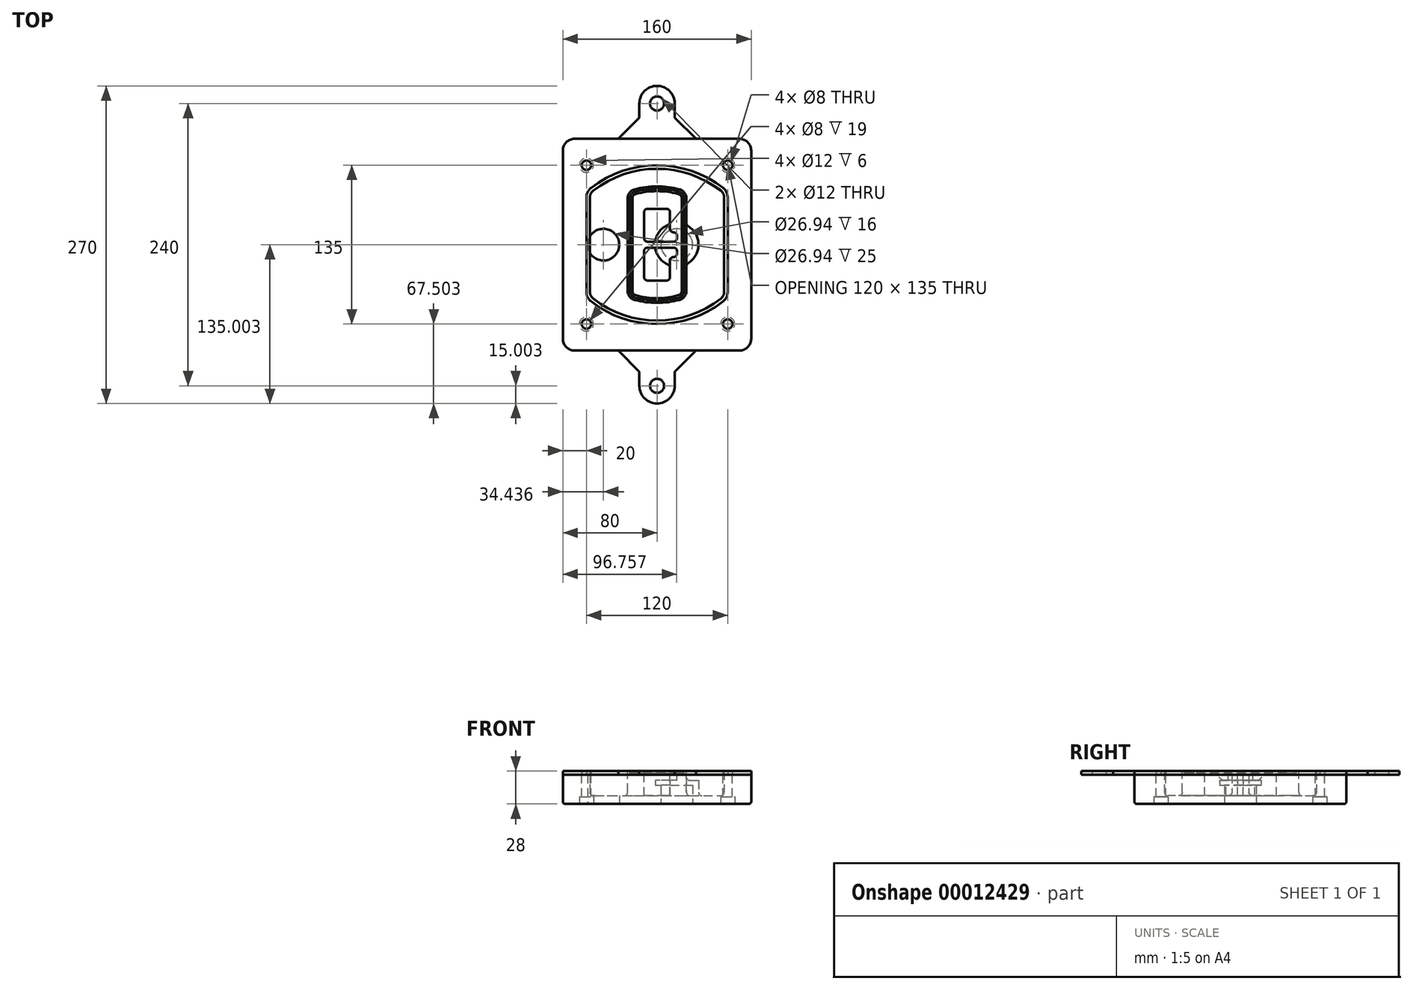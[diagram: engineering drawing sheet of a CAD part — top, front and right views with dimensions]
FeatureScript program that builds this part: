
annotation { "Feature Type Name" : "Feature", "Feature Type Description" : "" }
export const myFeature = defineFeature(function(context is Context, id is Id, definition is map)
    precondition{}
    {
        {
            var Q0;
            Q0=qCreatedBy(makeId("Top.planeOp"),FACE);
            var sketch = newSketch(context, id + "F0", { "sketchPlane" : qUnion([Q0])});
            skPoint(sketch, "E0.rect.middle", {"position": v(0, 0) * mm});
            skLineSegment(sketch, "E1.bottom", {"start": v(24.05, 28.38) * mm, "end": v(164.05, 28.38) * mm});
            skLineSegment(sketch, "E1.top", {"start": v(24.05, 208.38) * mm, "end": v(164.05, 208.38) * mm});
            skLineSegment(sketch, "E1.left", {"start": v(14.05, 38.38) * mm, "end": v(14.05, 198.38) * mm});
            skLineSegment(sketch, "E1.right", {"start": v(174.05, 38.38) * mm, "end": v(174.05, 198.38) * mm});
            skLineSegment(sketch, "E2", {"start": v(14.05, 208.38) * mm, "end": v(174.05, 28.38) * mm, "construction": true});
            skLineSegment(sketch, "E3", {"start": v(174.05, 208.38) * mm, "end": v(14.05, 28.38) * mm, "construction": true});
            skCircle(sketch, "E4", {"center": v(34.05, 185.88) * mm, "radius": 4 * mm});
            skCircle(sketch, "E5", {"center": v(154.05, 185.88) * mm, "radius": 4 * mm});
            skCircle(sketch, "E6", {"center": v(154.05, 50.88) * mm, "radius": 4 * mm});
            skCircle(sketch, "E7", {"center": v(34.05, 50.88) * mm, "radius": 4 * mm});
            skLineSegment(sketch, "E8", {"start": v(34.05, 185.88) * mm, "end": v(154.05, 185.88) * mm, "construction": true});
            skLineSegment(sketch, "E9", {"start": v(154.05, 185.88) * mm, "end": v(154.05, 50.88) * mm, "construction": true});
            skLineSegment(sketch, "E10", {"start": v(154.05, 50.88) * mm, "end": v(34.05, 50.88) * mm, "construction": true});
            skLineSegment(sketch, "E11", {"start": v(34.05, 50.88) * mm, "end": v(34.05, 185.88) * mm, "construction": true});
            skLineSegment(sketch, "E12", {"start": v(34.05, 158.68) * mm, "end": v(34.05, 78.09) * mm});
            skLineSegment(sketch, "E13", {"start": v(154.05, 158.68) * mm, "end": v(154.05, 78.09) * mm});
            skArc(sketch, "E14", {"start": v(150.2, 166.56) * mm, "mid": v(94.05, 185.88) * mm, "end": v(37.9, 166.56) * mm});
            skArc(sketch, "E15", {"start": v(37.9, 70.2) * mm, "mid": v(94.05, 50.88) * mm, "end": v(150.2, 70.2) * mm});
            skLineSegment(sketch, "E16", {"start": v(34.05, 118.38) * mm, "end": v(154.05, 118.38) * mm, "construction": true});
            skPoint(sketch, "E17.visualSharp", {"position": v(34.05, 73.38) * mm});
            skArc(sketch, "E17.filletArc", {"start": v(34.05, 78.09) * mm, "mid": v(35.06, 73.7) * mm, "end": v(37.9, 70.2) * mm});
            skPoint(sketch, "E18.visualSharp", {"position": v(34.05, 163.38) * mm});
            skArc(sketch, "E18.filletArc", {"start": v(37.9, 166.56) * mm, "mid": v(35.06, 163.06) * mm, "end": v(34.05, 158.68) * mm});
            skPoint(sketch, "E19.visualSharp", {"position": v(154.05, 163.38) * mm});
            skArc(sketch, "E19.filletArc", {"start": v(154.05, 158.68) * mm, "mid": v(153.04, 163.06) * mm, "end": v(150.2, 166.56) * mm});
            skPoint(sketch, "E20.visualSharp", {"position": v(154.05, 73.38) * mm});
            skArc(sketch, "E20.filletArc", {"start": v(150.2, 70.2) * mm, "mid": v(153.04, 73.7) * mm, "end": v(154.05, 78.09) * mm});
            skPoint(sketch, "E21.visualSharp", {"position": v(14.05, 208.38) * mm});
            skArc(sketch, "E21.filletArc", {"start": v(24.05, 208.38) * mm, "mid": v(16.98, 205.45) * mm, "end": v(14.05, 198.38) * mm});
            skPoint(sketch, "E22.visualSharp", {"position": v(174.05, 208.38) * mm});
            skArc(sketch, "E22.filletArc", {"start": v(174.05, 198.38) * mm, "mid": v(171.12, 205.45) * mm, "end": v(164.05, 208.38) * mm});
            skPoint(sketch, "E23.visualSharp", {"position": v(174.05, 28.38) * mm});
            skArc(sketch, "E23.filletArc", {"start": v(164.05, 28.38) * mm, "mid": v(171.12, 31.31) * mm, "end": v(174.05, 38.38) * mm});
            skPoint(sketch, "E24.visualSharp", {"position": v(14.05, 28.38) * mm});
            skArc(sketch, "E24.filletArc", {"start": v(14.05, 38.38) * mm, "mid": v(16.98, 31.31) * mm, "end": v(24.05, 28.38) * mm});
            skArc(sketch, "E25.0", {"start": v(151.05, 158.68) * mm, "mid": v(150.34, 161.75) * mm, "end": v(148.36, 164.2) * mm});
            skLineSegment(sketch, "E25.1", {"start": v(151.05, 158.68) * mm, "end": v(151.05, 78.09) * mm});
            skArc(sketch, "E25.2", {"start": v(148.36, 72.57) * mm, "mid": v(150.34, 75.02) * mm, "end": v(151.05, 78.09) * mm});
            skArc(sketch, "E25.3", {"start": v(39.74, 72.57) * mm, "mid": v(94.05, 53.88) * mm, "end": v(148.36, 72.57) * mm});
            skArc(sketch, "E25.4", {"start": v(37.05, 78.09) * mm, "mid": v(37.76, 75.02) * mm, "end": v(39.74, 72.57) * mm});
            skArc(sketch, "E25.5", {"start": v(148.36, 164.2) * mm, "mid": v(94.05, 182.88) * mm, "end": v(39.74, 164.2) * mm});
            skLineSegment(sketch, "E25.6", {"start": v(37.05, 158.68) * mm, "end": v(37.05, 78.09) * mm});
            skArc(sketch, "E25.7", {"start": v(39.74, 164.2) * mm, "mid": v(37.76, 161.75) * mm, "end": v(37.05, 158.68) * mm});
            skArc(sketch, "E26.0", {"start": v(35.43, 169.71) * mm, "mid": v(31.47, 164.82) * mm, "end": v(30.05, 158.68) * mm});
            skArc(sketch, "E26.1", {"start": v(152.67, 169.71) * mm, "mid": v(94.05, 189.88) * mm, "end": v(35.43, 169.71) * mm});
            skArc(sketch, "E26.2", {"start": v(158.05, 158.68) * mm, "mid": v(156.63, 164.82) * mm, "end": v(152.67, 169.71) * mm});
            skLineSegment(sketch, "E26.3", {"start": v(158.05, 158.68) * mm, "end": v(158.05, 78.09) * mm});
            skArc(sketch, "E26.4", {"start": v(152.67, 67.05) * mm, "mid": v(156.63, 71.95) * mm, "end": v(158.05, 78.09) * mm});
            skLineSegment(sketch, "E26.5", {"start": v(30.05, 158.68) * mm, "end": v(30.05, 78.09) * mm});
            skArc(sketch, "E26.6", {"start": v(35.43, 67.05) * mm, "mid": v(94.05, 46.88) * mm, "end": v(152.67, 67.05) * mm});
            skArc(sketch, "E26.7", {"start": v(30.05, 78.09) * mm, "mid": v(31.47, 71.95) * mm, "end": v(35.43, 67.05) * mm});
            skSolve(sketch);
        }
        {
            var Q0;
            Q0=makeQuery(id+"F0.imprint","IMPRINT",FACE,{"disambiguationData":[TD([[makeQuery(id+"F0.imprint","IMPRINT",EDGE,{"derivedFrom":sQuery(id+"F0.wireOp",EDGE,"E1.bottom")}),1.0]])]});
            var Q1;
            Q1=makeQuery(id+"F0.imprint","IMPRINT",FACE,{"disambiguationData":[TD([[makeQuery(id+"F0.imprint","IMPRINT",EDGE,{"derivedFrom":sQuery(id+"F0.wireOp",EDGE,"E12")}),1.0]])]});
            var Q2;
            Q2=makeQuery(id+"F0.imprint","IMPRINT",FACE,{"disambiguationData":[TD([[makeQuery(id+"F0.imprint","IMPRINT",EDGE,{"derivedFrom":sQuery(id+"F0.wireOp",EDGE,"E25.0")}),1.0]])]});
            var Q3;
            Q3=makeQuery(id+"F0.imprint","IMPRINT",FACE,{"disambiguationData":[TD([[makeQuery(id+"F0.imprint","IMPRINT",EDGE,{"derivedFrom":sQuery(id+"F0.wireOp",EDGE,"E12")}),-1.0]])]});
            extrude(context, id + "F1", {"entities" : qUnion([Q0, Q1, Q2, Q3]), "oppositeDirection" : true, "depth" : 25 * mm});
        }
        {
            var Q0;
            Q0=makeQuery(id+"F0.imprint","IMPRINT",FACE,{"disambiguationData":[TD([[makeQuery(id+"F0.imprint","IMPRINT",EDGE,{"derivedFrom":sQuery(id+"F0.wireOp",EDGE,"E12")}),1.0]])]});
            extrude(context, id + "F2", {"entities" : qUnion([Q0]), "operationType" : NewBodyOperationType.ADD, "depth" : 3 * mm});
        }
        {
            var Q0;
            Q0=makeQuery(id+"F0.imprint","IMPRINT",FACE,{"disambiguationData":[TD([[makeQuery(id+"F0.imprint","IMPRINT",EDGE,{"derivedFrom":sQuery(id+"F0.wireOp",EDGE,"E25.0")}),1.0]])]});
            extrude(context, id + "F3", {"entities" : qUnion([Q0]), "operationType" : NewBodyOperationType.REMOVE, "oppositeDirection" : true, "depth" : 18 * mm});
        }
        {
            var Q0;
            Q0=makeQuery(id+"F2.opExtrude","CAP_FACE",FACE,{"disambiguationData":[OSD([sQuery(id+"F0.wireOp",EDGE,"E12"),sQuery(id+"F0.wireOp",EDGE,"E13"),sQuery(id+"F0.wireOp",EDGE,"E14"),sQuery(id+"F0.wireOp",EDGE,"E15"),sQuery(id+"F0.wireOp",EDGE,"E17.filletArc"),sQuery(id+"F0.wireOp",EDGE,"E18.filletArc"),sQuery(id+"F0.wireOp",EDGE,"E19.filletArc"),sQuery(id+"F0.wireOp",EDGE,"E20.filletArc"),sQuery(id+"F0.wireOp",EDGE,"E25.0"),sQuery(id+"F0.wireOp",EDGE,"E25.1"),sQuery(id+"F0.wireOp",EDGE,"E25.2"),sQuery(id+"F0.wireOp",EDGE,"E25.3"),sQuery(id+"F0.wireOp",EDGE,"E25.4"),sQuery(id+"F0.wireOp",EDGE,"E25.5"),sQuery(id+"F0.wireOp",EDGE,"E25.6"),sQuery(id+"F0.wireOp",EDGE,"E25.7")])],"isStart":false});
            var sketch = newSketch(context, id + "F4", { "sketchPlane" : qUnion([Q0])});
            skArc(sketch, "E27.0", {"start": v(74.97, 71.41) * mm, "mid": v(94.05, 68.88) * mm, "end": v(113.13, 71.41) * mm});
            skArc(sketch, "E28.0", {"start": v(113.13, 165.35) * mm, "mid": v(94.05, 167.88) * mm, "end": v(74.97, 165.35) * mm});
            skLineSegment(sketch, "E29", {"start": v(69.05, 157.63) * mm, "end": v(69.05, 79.14) * mm});
            skLineSegment(sketch, "E30", {"start": v(119.05, 157.63) * mm, "end": v(119.05, 79.14) * mm});
            skLineSegment(sketch, "E31", {"start": v(69.05, 163.48) * mm, "end": v(119.05, 163.48) * mm, "construction": true});
            skLineSegment(sketch, "E32", {"start": v(69.05, 73.28) * mm, "end": v(119.05, 73.28) * mm, "construction": true});
            skPoint(sketch, "E33.visualSharp", {"position": v(69.05, 163.48) * mm});
            skArc(sketch, "E33.filletArc", {"start": v(74.97, 165.35) * mm, "mid": v(70.7, 162.5) * mm, "end": v(69.05, 157.63) * mm});
            skPoint(sketch, "E34.visualSharp", {"position": v(119.05, 163.48) * mm});
            skArc(sketch, "E34.filletArc", {"start": v(119.05, 157.63) * mm, "mid": v(117.4, 162.5) * mm, "end": v(113.13, 165.35) * mm});
            skPoint(sketch, "E35.visualSharp", {"position": v(119.05, 73.28) * mm});
            skArc(sketch, "E35.filletArc", {"start": v(113.13, 71.41) * mm, "mid": v(117.4, 74.27) * mm, "end": v(119.05, 79.14) * mm});
            skPoint(sketch, "E36.visualSharp", {"position": v(69.05, 73.28) * mm});
            skArc(sketch, "E36.filletArc", {"start": v(69.05, 79.14) * mm, "mid": v(70.7, 74.27) * mm, "end": v(74.97, 71.41) * mm});
            skArc(sketch, "E37.0", {"start": v(148.36, 164.2) * mm, "mid": v(94.05, 182.88) * mm, "end": v(39.74, 164.2) * mm});
            skArc(sketch, "E37.1", {"start": v(39.74, 164.2) * mm, "mid": v(37.76, 161.75) * mm, "end": v(37.05, 158.68) * mm});
            skLineSegment(sketch, "E37.2", {"start": v(37.05, 158.68) * mm, "end": v(37.05, 78.09) * mm});
            skArc(sketch, "E37.3", {"start": v(37.05, 78.09) * mm, "mid": v(37.76, 75.02) * mm, "end": v(39.74, 72.57) * mm});
            skArc(sketch, "E37.4", {"start": v(39.74, 72.57) * mm, "mid": v(94.05, 53.88) * mm, "end": v(148.36, 72.57) * mm});
            skArc(sketch, "E37.5", {"start": v(148.36, 72.57) * mm, "mid": v(150.34, 75.02) * mm, "end": v(151.05, 78.09) * mm});
            skLineSegment(sketch, "E37.6", {"start": v(151.05, 158.68) * mm, "end": v(151.05, 78.09) * mm});
            skArc(sketch, "E37.7", {"start": v(151.05, 158.68) * mm, "mid": v(150.34, 161.75) * mm, "end": v(148.36, 164.2) * mm});
            skLineSegment(sketch, "E38.0", {"start": v(117.05, 157.63) * mm, "end": v(117.05, 79.14) * mm});
            skArc(sketch, "E38.1", {"start": v(112.61, 73.34) * mm, "mid": v(115.81, 75.49) * mm, "end": v(117.05, 79.14) * mm});
            skArc(sketch, "E38.2", {"start": v(75.49, 73.34) * mm, "mid": v(94.05, 70.88) * mm, "end": v(112.61, 73.34) * mm});
            skArc(sketch, "E38.3", {"start": v(71.05, 79.14) * mm, "mid": v(72.29, 75.49) * mm, "end": v(75.49, 73.34) * mm});
            skLineSegment(sketch, "E38.4", {"start": v(71.05, 157.63) * mm, "end": v(71.05, 79.14) * mm});
            skArc(sketch, "E38.5", {"start": v(117.05, 157.63) * mm, "mid": v(115.81, 161.28) * mm, "end": v(112.61, 163.42) * mm});
            skArc(sketch, "E38.6", {"start": v(75.49, 163.42) * mm, "mid": v(72.29, 161.28) * mm, "end": v(71.05, 157.63) * mm});
            skArc(sketch, "E38.7", {"start": v(112.61, 163.42) * mm, "mid": v(94.05, 165.88) * mm, "end": v(75.49, 163.42) * mm});
            skArc(sketch, "E39.0", {"start": v(115.05, 157.63) * mm, "mid": v(114.23, 160.06) * mm, "end": v(112.1, 161.5) * mm});
            skLineSegment(sketch, "E39.1", {"start": v(115.05, 157.63) * mm, "end": v(115.05, 79.14) * mm});
            skArc(sketch, "E39.2", {"start": v(112.1, 75.27) * mm, "mid": v(114.23, 76.7) * mm, "end": v(115.05, 79.14) * mm});
            skArc(sketch, "E39.3", {"start": v(76, 75.27) * mm, "mid": v(94.05, 72.88) * mm, "end": v(112.1, 75.27) * mm});
            skArc(sketch, "E39.4", {"start": v(73.05, 79.14) * mm, "mid": v(73.87, 76.7) * mm, "end": v(76, 75.27) * mm});
            skArc(sketch, "E39.5", {"start": v(112.1, 161.5) * mm, "mid": v(94.05, 163.88) * mm, "end": v(76, 161.5) * mm});
            skLineSegment(sketch, "E39.6", {"start": v(73.05, 157.63) * mm, "end": v(73.05, 79.14) * mm});
            skArc(sketch, "E39.7", {"start": v(76, 161.5) * mm, "mid": v(73.87, 160.06) * mm, "end": v(73.05, 157.63) * mm});
            skLineSegment(sketch, "E40", {"start": v(69.05, 118.38) * mm, "end": v(119.05, 118.38) * mm, "construction": true});
            skLineSegment(sketch, "E41", {"start": v(83.05, 123.88) * mm, "end": v(83.05, 145.88) * mm});
            skLineSegment(sketch, "E42", {"start": v(86.05, 148.88) * mm, "end": v(102.05, 148.88) * mm});
            skLineSegment(sketch, "E43", {"start": v(105.05, 145.88) * mm, "end": v(105.05, 131.88) * mm});
            skLineSegment(sketch, "E44", {"start": v(108.05, 128.88) * mm, "end": v(108.05, 128.88) * mm});
            skLineSegment(sketch, "E45", {"start": v(111.05, 125.88) * mm, "end": v(111.05, 123.88) * mm});
            skLineSegment(sketch, "E46", {"start": v(108.05, 120.88) * mm, "end": v(86.05, 120.88) * mm});
            skPoint(sketch, "E47.visualSharp", {"position": v(83.05, 148.88) * mm});
            skArc(sketch, "E47.filletArc", {"start": v(86.05, 148.88) * mm, "mid": v(83.93, 148) * mm, "end": v(83.05, 145.88) * mm});
            skPoint(sketch, "E48.visualSharp", {"position": v(105.05, 148.88) * mm});
            skArc(sketch, "E48.filletArc", {"start": v(105.05, 145.88) * mm, "mid": v(104.17, 148) * mm, "end": v(102.05, 148.88) * mm});
            skPoint(sketch, "E49.visualSharp", {"position": v(105.05, 128.88) * mm});
            skArc(sketch, "E49.filletArc", {"start": v(105.05, 131.88) * mm, "mid": v(105.93, 129.76) * mm, "end": v(108.05, 128.88) * mm});
            skPoint(sketch, "E50.visualSharp", {"position": v(111.05, 128.88) * mm});
            skArc(sketch, "E50.filletArc", {"start": v(111.05, 125.88) * mm, "mid": v(110.17, 128) * mm, "end": v(108.05, 128.88) * mm});
            skPoint(sketch, "E51.visualSharp", {"position": v(111.05, 120.88) * mm});
            skArc(sketch, "E51.filletArc", {"start": v(108.05, 120.88) * mm, "mid": v(110.17, 121.76) * mm, "end": v(111.05, 123.88) * mm});
            skPoint(sketch, "E52.visualSharp", {"position": v(83.05, 120.88) * mm});
            skArc(sketch, "E52.filletArc", {"start": v(83.05, 123.88) * mm, "mid": v(83.93, 121.76) * mm, "end": v(86.05, 120.88) * mm});
            skLineSegment(sketch, "E53.0.MirrorCS", {"start": v(108.05, 115.88) * mm, "end": v(86.05, 115.88) * mm});
            skArc(sketch, "E54.0.MirrorCS", {"start": v(83.05, 112.88) * mm, "mid": v(83.93, 115) * mm, "end": v(86.05, 115.88) * mm});
            skLineSegment(sketch, "E55.0.MirrorCS", {"start": v(83.05, 112.88) * mm, "end": v(83.05, 90.88) * mm});
            skArc(sketch, "E56.0.MirrorCS", {"start": v(86.05, 87.88) * mm, "mid": v(83.93, 88.76) * mm, "end": v(83.05, 90.88) * mm});
            skLineSegment(sketch, "E57.0.MirrorCS", {"start": v(86.05, 87.88) * mm, "end": v(102.05, 87.88) * mm});
            skArc(sketch, "E58.0.MirrorCS", {"start": v(105.05, 90.88) * mm, "mid": v(104.17, 88.76) * mm, "end": v(102.05, 87.88) * mm});
            skLineSegment(sketch, "E59.0.MirrorCS", {"start": v(105.05, 90.88) * mm, "end": v(105.05, 104.88) * mm});
            skArc(sketch, "E60.0.MirrorCS", {"start": v(105.05, 104.88) * mm, "mid": v(105.93, 107) * mm, "end": v(108.05, 107.88) * mm});
            skArc(sketch, "E61.0.MirrorCS", {"start": v(111.05, 110.88) * mm, "mid": v(110.17, 108.76) * mm, "end": v(108.05, 107.88) * mm});
            skLineSegment(sketch, "E62.0.MirrorCS", {"start": v(111.05, 110.88) * mm, "end": v(111.05, 112.88) * mm});
            skArc(sketch, "E63.0.MirrorCS", {"start": v(108.05, 115.88) * mm, "mid": v(110.17, 115) * mm, "end": v(111.05, 112.88) * mm});
            skSolve(sketch);
        }
        {
            var Q0;
            Q0=makeQuery(id+"F4.imprint","IMPRINT",FACE,{"disambiguationData":[TD([[makeQuery(id+"F4.imprint","IMPRINT",EDGE,{"derivedFrom":sQuery(id+"F4.wireOp",EDGE,"E27.0")}),1.0]])]});
            var Q1;
            Q1=makeQuery(id+"F4.imprint","IMPRINT",FACE,{"disambiguationData":[TD([[makeQuery(id+"F4.imprint","IMPRINT",EDGE,{"derivedFrom":sQuery(id+"F4.wireOp",EDGE,"E38.0")}),-1.0]])]});
            var Q2;
            Q2=makeQuery(id+"F4.imprint","IMPRINT",FACE,{"disambiguationData":[TD([[makeQuery(id+"F4.imprint","IMPRINT",EDGE,{"derivedFrom":sQuery(id+"F4.wireOp",EDGE,"E39.0")}),1.0]])]});
            extrude(context, id + "F5", {"entities" : qUnion([Q0, Q1, Q2]), "operationType" : NewBodyOperationType.ADD, "endBound" : BoundingType.UP_TO_NEXT, "oppositeDirection" : true, "depth" : 25 * mm});
        }
        {
            var Q0;
            Q0=makeQuery(id+"F4.imprint","IMPRINT",FACE,{"disambiguationData":[TD([[makeQuery(id+"F4.imprint","IMPRINT",EDGE,{"derivedFrom":sQuery(id+"F4.wireOp",EDGE,"E38.0")}),-1.0]])]});
            extrude(context, id + "F6", {"entities" : qUnion([Q0]), "operationType" : NewBodyOperationType.REMOVE, "oppositeDirection" : true, "depth" : 2 * mm});
        }
        {
            var Q0;
            Q0=makeQuery(id+"F1.opExtrude","CAP_FACE",FACE,{"disambiguationData":[OSD([sQuery(id+"F0.wireOp",EDGE,"E1.bottom"),sQuery(id+"F0.wireOp",EDGE,"E1.top"),sQuery(id+"F0.wireOp",EDGE,"E1.left"),sQuery(id+"F0.wireOp",EDGE,"E1.right"),sQuery(id+"F0.wireOp",EDGE,"E4"),sQuery(id+"F0.wireOp",EDGE,"E5"),sQuery(id+"F0.wireOp",EDGE,"E6"),sQuery(id+"F0.wireOp",EDGE,"E7"),sQuery(id+"F0.wireOp",EDGE,"E21.filletArc"),sQuery(id+"F0.wireOp",EDGE,"E22.filletArc"),sQuery(id+"F0.wireOp",EDGE,"E23.filletArc"),sQuery(id+"F0.wireOp",EDGE,"E24.filletArc")])],"isStart":false});
            var sketch = newSketch(context, id + "F7", { "sketchPlane" : qUnion([Q0])});
            skCircle(sketch, "E64", {"center": v(110.8, -118.38) * mm, "radius": 13.47 * mm});
            skCircle(sketch, "E65", {"center": v(48.49, -118.38) * mm, "radius": 13.47 * mm});
            skLineSegment(sketch, "E66", {"start": v(174.05, -118.38) * mm, "end": v(14.05, -118.38) * mm});
            skCircle(sketch, "E67", {"center": v(110.8, -118.38) * mm, "radius": 18.47 * mm});
            skCircle(sketch, "E68", {"center": v(154.05, -185.88) * mm, "radius": 6 * mm});
            skCircle(sketch, "E69", {"center": v(34.05, -185.88) * mm, "radius": 6 * mm});
            skCircle(sketch, "E70", {"center": v(34.05, -50.88) * mm, "radius": 6 * mm});
            skCircle(sketch, "E71", {"center": v(154.05, -50.88) * mm, "radius": 6 * mm});
            skSolve(sketch);
        }
        {
            var Q0;
            {var subQ1=sQuery(id+"F7.wireOp",EDGE,"E66");var subQ4=sQuery(id+"F7.wireOp",EDGE,"E64");var subQ6=makeQuery(id+"F7.imprint","INTERSECT",VERTEX,{"disambiguationData":[OD(0.0)],"derivedFrom":[subQ4,subQ1]});Q0=makeQuery(id+"F7.imprint","IMPRINT",FACE,{"disambiguationData":[TD([[makeQuery(id+"F7.imprint","IMPRINT",EDGE,{"disambiguationData":[TD([[subQ6,-1.0]])],"derivedFrom":subQ4}),-1.0]])]});}
            var Q1;
            {var subQ0=sQuery(id+"F7.wireOp",EDGE,"E66");var subQ1=sQuery(id+"F7.wireOp",EDGE,"E64");var subQ3=makeQuery(id+"F7.imprint","INTERSECT",VERTEX,{"disambiguationData":[OD(0.0)],"derivedFrom":[subQ1,subQ0]});Q1=makeQuery(id+"F7.imprint","IMPRINT",FACE,{"disambiguationData":[TD([[makeQuery(id+"F7.imprint","IMPRINT",EDGE,{"disambiguationData":[TD([[subQ3,-1.0]])],"derivedFrom":subQ1}),1.0]])]});}
            var Q2;
            {var subQ0=sQuery(id+"F7.wireOp",EDGE,"E66");var subQ1=sQuery(id+"F7.wireOp",EDGE,"E64");var subQ3=makeQuery(id+"F7.imprint","INTERSECT",VERTEX,{"disambiguationData":[OD(0.0)],"derivedFrom":[subQ1,subQ0]});Q2=makeQuery(id+"F7.imprint","IMPRINT",FACE,{"disambiguationData":[TD([[makeQuery(id+"F7.imprint","IMPRINT",EDGE,{"disambiguationData":[TD([[subQ3,1.0]])],"derivedFrom":subQ1}),1.0]])]});}
            var Q3;
            {var subQ1=sQuery(id+"F7.wireOp",EDGE,"E66");var subQ4=sQuery(id+"F7.wireOp",EDGE,"E64");var subQ6=makeQuery(id+"F7.imprint","INTERSECT",VERTEX,{"disambiguationData":[OD(0.0)],"derivedFrom":[subQ4,subQ1]});Q3=makeQuery(id+"F7.imprint","IMPRINT",FACE,{"disambiguationData":[TD([[makeQuery(id+"F7.imprint","IMPRINT",EDGE,{"disambiguationData":[TD([[subQ6,1.0]])],"derivedFrom":subQ4}),-1.0]])]});}
            extrude(context, id + "F8", {"entities" : qUnion([Q0, Q1, Q2, Q3]), "operationType" : NewBodyOperationType.ADD, "oppositeDirection" : true, "depth" : 20 * mm});
        }
        {
            var Q0;
            {var subQ0=sQuery(id+"F7.wireOp",EDGE,"E66");var subQ1=sQuery(id+"F7.wireOp",EDGE,"E64");var subQ3=makeQuery(id+"F7.imprint","INTERSECT",VERTEX,{"disambiguationData":[OD(0.0)],"derivedFrom":[subQ1,subQ0]});Q0=makeQuery(id+"F7.imprint","IMPRINT",FACE,{"disambiguationData":[TD([[makeQuery(id+"F7.imprint","IMPRINT",EDGE,{"disambiguationData":[TD([[subQ3,-1.0]])],"derivedFrom":subQ1}),1.0]])]});}
            var Q1;
            {var subQ0=sQuery(id+"F7.wireOp",EDGE,"E66");var subQ1=sQuery(id+"F7.wireOp",EDGE,"E64");var subQ3=makeQuery(id+"F7.imprint","INTERSECT",VERTEX,{"disambiguationData":[OD(0.0)],"derivedFrom":[subQ1,subQ0]});Q1=makeQuery(id+"F7.imprint","IMPRINT",FACE,{"disambiguationData":[TD([[makeQuery(id+"F7.imprint","IMPRINT",EDGE,{"disambiguationData":[TD([[subQ3,1.0]])],"derivedFrom":subQ1}),1.0]])]});}
            extrude(context, id + "F9", {"entities" : qUnion([Q0, Q1]), "operationType" : NewBodyOperationType.REMOVE, "oppositeDirection" : true, "depth" : 16 * mm});
        }
        {
            var Q0;
            {var subQ0=sQuery(id+"F7.wireOp",EDGE,"E66");var subQ1=sQuery(id+"F7.wireOp",EDGE,"E65");var subQ3=makeQuery(id+"F7.imprint","INTERSECT",VERTEX,{"disambiguationData":[OD(0.0)],"derivedFrom":[subQ1,subQ0]});Q0=makeQuery(id+"F7.imprint","IMPRINT",FACE,{"disambiguationData":[TD([[makeQuery(id+"F7.imprint","IMPRINT",EDGE,{"disambiguationData":[TD([[subQ3,-1.0]])],"derivedFrom":subQ1}),1.0]])]});}
            var Q1;
            {var subQ0=sQuery(id+"F7.wireOp",EDGE,"E66");var subQ1=sQuery(id+"F7.wireOp",EDGE,"E65");var subQ3=makeQuery(id+"F7.imprint","INTERSECT",VERTEX,{"disambiguationData":[OD(0.0)],"derivedFrom":[subQ1,subQ0]});Q1=makeQuery(id+"F7.imprint","IMPRINT",FACE,{"disambiguationData":[TD([[makeQuery(id+"F7.imprint","IMPRINT",EDGE,{"disambiguationData":[TD([[subQ3,1.0]])],"derivedFrom":subQ1}),1.0]])]});}
            extrude(context, id + "F10", {"entities" : qUnion([Q0, Q1]), "operationType" : NewBodyOperationType.REMOVE, "oppositeDirection" : true, "depth" : 25 * mm});
        }
        {
            var Q0;
            Q0=makeQuery(id+"F7.imprint","IMPRINT",FACE,{"disambiguationData":[TD([[makeQuery(id+"F7.imprint","IMPRINT",EDGE,{"derivedFrom":sQuery(id+"F7.wireOp",EDGE,"E68")}),1.0]])]});
            var Q1;
            Q1=makeQuery(id+"F7.imprint","IMPRINT",FACE,{"disambiguationData":[TD([[makeQuery(id+"F7.imprint","IMPRINT",EDGE,{"derivedFrom":makeQuery(id+"F1.opExtrude","CAP_EDGE",EDGE,{"disambiguationData":[OSD([sQuery(id+"F0.wireOp",EDGE,"E5")])],"isStart":false})}),-1.0]])]});
            var Q2;
            Q2=makeQuery(id+"F7.imprint","IMPRINT",FACE,{"disambiguationData":[TD([[makeQuery(id+"F7.imprint","IMPRINT",EDGE,{"derivedFrom":sQuery(id+"F7.wireOp",EDGE,"E69")}),1.0]])]});
            var Q3;
            Q3=makeQuery(id+"F7.imprint","IMPRINT",FACE,{"disambiguationData":[TD([[makeQuery(id+"F7.imprint","IMPRINT",EDGE,{"derivedFrom":makeQuery(id+"F1.opExtrude","CAP_EDGE",EDGE,{"disambiguationData":[OSD([sQuery(id+"F0.wireOp",EDGE,"E4")])],"isStart":false})}),-1.0]])]});
            var Q4;
            Q4=makeQuery(id+"F7.imprint","IMPRINT",FACE,{"disambiguationData":[TD([[makeQuery(id+"F7.imprint","IMPRINT",EDGE,{"derivedFrom":sQuery(id+"F7.wireOp",EDGE,"E70")}),1.0]])]});
            var Q5;
            Q5=makeQuery(id+"F7.imprint","IMPRINT",FACE,{"disambiguationData":[TD([[makeQuery(id+"F7.imprint","IMPRINT",EDGE,{"derivedFrom":makeQuery(id+"F1.opExtrude","CAP_EDGE",EDGE,{"disambiguationData":[OSD([sQuery(id+"F0.wireOp",EDGE,"E7")])],"isStart":false})}),-1.0]])]});
            var Q6;
            Q6=makeQuery(id+"F7.imprint","IMPRINT",FACE,{"disambiguationData":[TD([[makeQuery(id+"F7.imprint","IMPRINT",EDGE,{"derivedFrom":sQuery(id+"F7.wireOp",EDGE,"E71")}),1.0]])]});
            var Q7;
            Q7=makeQuery(id+"F7.imprint","IMPRINT",FACE,{"disambiguationData":[TD([[makeQuery(id+"F7.imprint","IMPRINT",EDGE,{"derivedFrom":makeQuery(id+"F1.opExtrude","CAP_EDGE",EDGE,{"disambiguationData":[OSD([sQuery(id+"F0.wireOp",EDGE,"E6")])],"isStart":false})}),-1.0]])]});
            extrude(context, id + "F11", {"entities" : qUnion([Q0, Q1, Q2, Q3, Q4, Q5, Q6, Q7]), "operationType" : NewBodyOperationType.REMOVE, "oppositeDirection" : true, "depth" : 6 * mm});
        }
        {
            var Q0;
            Q0=makeQuery(id+"F9.boolean.opBoolean","COPY",FACE,{"derivedFrom":makeQuery(id+"F9.opExtrude","CAP_FACE",FACE,{"disambiguationData":[OSD([sQuery(id+"F7.wireOp",EDGE,"E64")])],"isStart":false})});
            var sketch = newSketch(context, id + "F12", { "sketchPlane" : qUnion([Q0])});
            skArc(sketch, "E72.0", {"start": v(105.05, -100.83) * mm, "mid": v(96.62, -106.56) * mm, "end": v(92.5, -115.88) * mm});
            skArc(sketch, "E72.1", {"start": v(92.5, -120.88) * mm, "mid": v(96.62, -130.2) * mm, "end": v(105.05, -135.93) * mm});
            skLineSegment(sketch, "E73", {"start": v(92.5, -120.88) * mm, "end": v(108.05, -120.88) * mm});
            skLineSegment(sketch, "E74.0", {"start": v(108.05, -115.88) * mm, "end": v(92.5, -115.88) * mm});
            skArc(sketch, "E74.1", {"start": v(108.05, -115.88) * mm, "mid": v(110.17, -115) * mm, "end": v(111.05, -112.88) * mm});
            skLineSegment(sketch, "E74.2", {"start": v(111.05, -110.88) * mm, "end": v(111.05, -112.88) * mm});
            skArc(sketch, "E74.3", {"start": v(111.05, -110.88) * mm, "mid": v(110.17, -108.76) * mm, "end": v(108.05, -107.88) * mm});
            skArc(sketch, "E74.4", {"start": v(105.05, -104.88) * mm, "mid": v(105.93, -107) * mm, "end": v(108.05, -107.88) * mm});
            skLineSegment(sketch, "E74.5", {"start": v(105.05, -100.83) * mm, "end": v(105.05, -104.88) * mm});
            skLineSegment(sketch, "E74.7", {"start": v(108.05, -120.88) * mm, "end": v(92.5, -120.88) * mm});
            skArc(sketch, "E74.8", {"start": v(108.05, -120.88) * mm, "mid": v(110.17, -121.76) * mm, "end": v(111.05, -123.88) * mm});
            skLineSegment(sketch, "E74.9", {"start": v(111.05, -125.88) * mm, "end": v(111.05, -123.88) * mm});
            skArc(sketch, "E74.10", {"start": v(111.05, -125.88) * mm, "mid": v(110.17, -128) * mm, "end": v(108.05, -128.88) * mm});
            skArc(sketch, "E74.11", {"start": v(105.05, -131.88) * mm, "mid": v(105.93, -129.76) * mm, "end": v(108.05, -128.88) * mm});
            skLineSegment(sketch, "E74.12", {"start": v(105.05, -135.93) * mm, "end": v(105.05, -131.88) * mm});
            skPoint(sketch, "E75.orphan", {"position": v(105.05, -145.88) * mm});
            skPoint(sketch, "E76.orphan", {"position": v(86.05, -120.88) * mm});
            skPoint(sketch, "E77.orphan", {"position": v(86.05, -115.88) * mm});
            skPoint(sketch, "E78.orphan", {"position": v(105.05, -90.88) * mm});
            skSolve(sketch);
        }
        {
            var Q0;
            {var subQ7=sQuery(id+"F12.wireOp",EDGE,"E72.0");var subQ14=sQuery(id+"F12.wireOp",EDGE,"E72.1");var subQ16=sQuery(id+"F12.wireOp",EDGE,"E74.1");var subQ18=sQuery(id+"F12.wireOp",EDGE,"E74.8");Q0=qUnion([makeQuery(id+"F12.imprint","IMPRINT",FACE,{"disambiguationData":[TD([[makeQuery(id+"F12.imprint","IMPRINT",EDGE,{"derivedFrom":subQ7}),1.0]])]}),makeQuery(id+"F12.imprint","IMPRINT",FACE,{"disambiguationData":[TD([[makeQuery(id+"F12.imprint","IMPRINT",EDGE,{"derivedFrom":subQ14}),1.0]])]}),makeQuery(id+"F12.imprint","IMPRINT",FACE,{"disambiguationData":[TD([[makeQuery(id+"F12.imprint","IMPRINT",EDGE,{"derivedFrom":subQ16}),1.0]])]}),makeQuery(id+"F12.imprint","IMPRINT",FACE,{"disambiguationData":[TD([[makeQuery(id+"F12.imprint","IMPRINT",EDGE,{"derivedFrom":subQ18}),-1.0]])]})]);}
            var Q1;
            Q1=makeQuery(id+"F5.boolean.opBoolean","SPLIT",FACE,{"disambiguationData":[TD([makeQuery(id+"F5.opExtrude","SWEPT_FACE",FACE,{"disambiguationData":[OSD([sQuery(id+"F4.wireOp",EDGE,"E41")])]})])],"derivedFrom":makeQuery(id+"F3.boolean.opBoolean","COPY",FACE,{"derivedFrom":makeQuery(id+"F3.opExtrude","CAP_FACE",FACE,{"disambiguationData":[OSD([sQuery(id+"F0.wireOp",EDGE,"E25.0"),sQuery(id+"F0.wireOp",EDGE,"E25.1"),sQuery(id+"F0.wireOp",EDGE,"E25.2"),sQuery(id+"F0.wireOp",EDGE,"E25.3"),sQuery(id+"F0.wireOp",EDGE,"E25.4"),sQuery(id+"F0.wireOp",EDGE,"E25.5"),sQuery(id+"F0.wireOp",EDGE,"E25.6"),sQuery(id+"F0.wireOp",EDGE,"E25.7")])],"isStart":false})})});
            extrude(context, id + "F13", {"entities" : qUnion([Q0]), "operationType" : NewBodyOperationType.REMOVE, "endBound" : BoundingType.UP_TO_SURFACE, "endBoundEntityFace" : qUnion([Q1]), "depth" : 25 * mm});
        }
        {
            var Q0;
            Q0=makeQuery(id+"F3.boolean.opBoolean","COPY",EDGE,{"derivedFrom":makeQuery(id+"F3.opExtrude","CAP_EDGE",EDGE,{"disambiguationData":[OSD([sQuery(id+"F0.wireOp",EDGE,"E25.6")])],"isStart":false})});
            var Q1;
            Q1=makeQuery(id+"F8.boolean.opBoolean","INTERSECT",EDGE,{"derivedFrom":[makeQuery(id+"F5.opExtrude","SWEPT_FACE",FACE,{"disambiguationData":[OSD([sQuery(id+"F4.wireOp",EDGE,"E30")])]}),makeQuery(id+"F8.opExtrude","CAP_FACE",FACE,{"disambiguationData":[OSD([sQuery(id+"F7.wireOp",EDGE,"E67")])],"isStart":false})]});
            var Q2;
            Q2=makeQuery(id+"F8.boolean.opBoolean","INTERSECT",EDGE,{"disambiguationData":[OD(1.0)],"derivedFrom":[makeQuery(id+"F5.opExtrude","SWEPT_FACE",FACE,{"disambiguationData":[OSD([sQuery(id+"F4.wireOp",EDGE,"E30")])]}),makeQuery(id+"F8.opExtrude","SWEPT_FACE",FACE,{"disambiguationData":[OSD([sQuery(id+"F7.wireOp",EDGE,"E67")])]})]});
            var Q3;
            {var subQ0=sQuery(id+"F4.wireOp",EDGE,"E30");Q3=makeQuery(id+"F8.boolean.opBoolean","SPLIT",EDGE,{"disambiguationData":[TD([makeQuery(id+"F5.opExtrude","SWEPT_FACE",FACE,{"disambiguationData":[OSD([sQuery(id+"F4.wireOp",EDGE,"E35.filletArc")])]})])],"derivedFrom":makeQuery(id+"F5.opExtrude","CAP_EDGE",EDGE,{"disambiguationData":[OSD([subQ0])],"isStart":false})});}
            var Q4;
            {var subQ0=sQuery(id+"F0.wireOp",EDGE,"E25.7");var subQ1=sQuery(id+"F0.wireOp",EDGE,"E25.1");var subQ2=sQuery(id+"F0.wireOp",EDGE,"E25.6");var subQ3=sQuery(id+"F0.wireOp",EDGE,"E25.5");var subQ4=sQuery(id+"F0.wireOp",EDGE,"E25.4");var subQ5=sQuery(id+"F0.wireOp",EDGE,"E25.0");var subQ6=sQuery(id+"F0.wireOp",EDGE,"E25.2");var subQ7=sQuery(id+"F0.wireOp",EDGE,"E25.3");Q4=makeQuery(id+"F8.boolean.opBoolean","INTERSECT",EDGE,{"derivedFrom":[makeQuery(id+"F5.boolean.opBoolean","SPLIT",FACE,{"disambiguationData":[TD([makeQuery(id+"F2.opExtrude","SWEPT_FACE",FACE,{"disambiguationData":[OSD([subQ5])]})])],"derivedFrom":makeQuery(id+"F3.boolean.opBoolean","COPY",FACE,{"derivedFrom":makeQuery(id+"F3.opExtrude","CAP_FACE",FACE,{"disambiguationData":[OSD([subQ5,subQ1,subQ6,subQ7,subQ4,subQ3,subQ2,subQ0])],"isStart":false})})}),makeQuery(id+"F8.opExtrude","SWEPT_FACE",FACE,{"disambiguationData":[OSD([sQuery(id+"F7.wireOp",EDGE,"E67")])]})]});}
            var Q5;
            Q5=makeQuery(id+"F8.boolean.opBoolean","INTERSECT",EDGE,{"disambiguationData":[OD(0.0)],"derivedFrom":[makeQuery(id+"F5.opExtrude","SWEPT_FACE",FACE,{"disambiguationData":[OSD([sQuery(id+"F4.wireOp",EDGE,"E30")])]}),makeQuery(id+"F8.opExtrude","SWEPT_FACE",FACE,{"disambiguationData":[OSD([sQuery(id+"F7.wireOp",EDGE,"E67")])]})]});
            fillet(context, id + "F14", {"entities" : qUnion([Q0, Q1, Q2, Q3, Q4, Q5]), "radius" : 3 * mm, "tangentPropagation" : true, "allowEdgeOverflow" : false});
        }
        {
            var Q0;
            Q0=makeQuery(id+"F1.opExtrude","CAP_EDGE",EDGE,{"disambiguationData":[OSD([sQuery(id+"F0.wireOp",EDGE,"E1.bottom")])],"isStart":false});
            fillet(context, id + "F15", {"entities" : qUnion([Q0]), "radius" : 2 * mm, "tangentPropagation" : true, "allowEdgeOverflow" : false});
        }
        {
            var Q0;
            {var subQ0=sQuery(id+"F0.wireOp",EDGE,"E1.bottom");var subQ1=sQuery(id+"F0.wireOp",EDGE,"E1.top");var subQ2=sQuery(id+"F0.wireOp",EDGE,"E1.left");var subQ3=sQuery(id+"F0.wireOp",EDGE,"E1.right");var subQ4=sQuery(id+"F0.wireOp",EDGE,"E4");var subQ5=sQuery(id+"F0.wireOp",EDGE,"E5");var subQ6=sQuery(id+"F0.wireOp",EDGE,"E6");var subQ7=sQuery(id+"F0.wireOp",EDGE,"E7");var subQ8=sQuery(id+"F0.wireOp",EDGE,"E21.filletArc");var subQ9=sQuery(id+"F0.wireOp",EDGE,"E22.filletArc");var subQ10=sQuery(id+"F0.wireOp",EDGE,"E23.filletArc");var subQ11=sQuery(id+"F0.wireOp",EDGE,"E24.filletArc");Q0=makeQuery(id+"F2.boolean.opBoolean","SPLIT",FACE,{"disambiguationData":[TD([makeQuery(id+"F1.opExtrude","SWEPT_FACE",FACE,{"disambiguationData":[OSD([subQ0])]})])],"derivedFrom":makeQuery(id+"F1.opExtrude","CAP_FACE",FACE,{"disambiguationData":[OSD([subQ0,subQ1,subQ2,subQ3,subQ4,subQ5,subQ6,subQ7,subQ8,subQ9,subQ10,subQ11])],"isStart":true})});}
            var sketch = newSketch(context, id + "F16", { "sketchPlane" : qUnion([Q0])});
            skLineSegment(sketch, "E79", {"start": v(61.05, 208.38) * mm, "end": v(79.05, 226.38) * mm});
            skLineSegment(sketch, "E80", {"start": v(79.05, 226.38) * mm, "end": v(79.05, 238.38) * mm});
            skLineSegment(sketch, "E81", {"start": v(109.05, 238.38) * mm, "end": v(109.05, 226.38) * mm});
            skLineSegment(sketch, "E82", {"start": v(109.05, 226.38) * mm, "end": v(127.05, 208.38) * mm});
            skArc(sketch, "E83", {"start": v(109.05, 238.38) * mm, "mid": v(94.05, 253.38) * mm, "end": v(79.05, 238.38) * mm});
            skCircle(sketch, "E84", {"center": v(94.05, 238.38) * mm, "radius": 6 * mm});
            skLineSegment(sketch, "E85", {"start": v(94.05, 238.38) * mm, "end": v(94.05, 208.38) * mm, "construction": true});
            skLineSegment(sketch, "E86", {"start": v(14.05, 118.38) * mm, "end": v(174.05, 118.38) * mm, "construction": true});
            skLineSegment(sketch, "E87.0.MirrorCS", {"start": v(61.05, 28.38) * mm, "end": v(79.05, 10.38) * mm});
            skArc(sketch, "E88.0.MirrorCS", {"start": v(109.05, -1.62) * mm, "mid": v(94.05, -16.62) * mm, "end": v(79.05, -1.62) * mm});
            skCircle(sketch, "E88.1.MirrorC", {"center": v(94.05, -1.62) * mm, "radius": 6 * mm});
            skLineSegment(sketch, "E89.0.MirrorCS", {"start": v(109.05, -1.62) * mm, "end": v(109.05, 10.38) * mm});
            skLineSegment(sketch, "E90.0.MirrorCS", {"start": v(109.05, 10.38) * mm, "end": v(127.05, 28.38) * mm});
            skLineSegment(sketch, "E91.0.MirrorCS", {"start": v(79.05, 10.38) * mm, "end": v(79.05, -1.62) * mm});
            skLineSegment(sketch, "E92", {"start": v(61.05, 208.38) * mm, "end": v(127.05, 208.38) * mm});
            skLineSegment(sketch, "E93.0.MirrorCS", {"start": v(61.05, 28.38) * mm, "end": v(127.05, 28.38) * mm});
            skLineSegment(sketch, "E94.0.MirrorCS", {"start": v(94.05, -1.62) * mm, "end": v(94.05, 28.38) * mm, "construction": true});
            skSolve(sketch);
        }
        {
            var Q0;
            Q0 = qSketchRegion(id + "F16", true);
            var Q1;
            Q1=makeQuery(id+"F2.opExtrude","CAP_FACE",FACE,{"disambiguationData":[OSD([sQuery(id+"F0.wireOp",EDGE,"E12"),sQuery(id+"F0.wireOp",EDGE,"E13"),sQuery(id+"F0.wireOp",EDGE,"E14"),sQuery(id+"F0.wireOp",EDGE,"E15"),sQuery(id+"F0.wireOp",EDGE,"E17.filletArc"),sQuery(id+"F0.wireOp",EDGE,"E18.filletArc"),sQuery(id+"F0.wireOp",EDGE,"E19.filletArc"),sQuery(id+"F0.wireOp",EDGE,"E20.filletArc"),sQuery(id+"F0.wireOp",EDGE,"E25.0"),sQuery(id+"F0.wireOp",EDGE,"E25.1"),sQuery(id+"F0.wireOp",EDGE,"E25.2"),sQuery(id+"F0.wireOp",EDGE,"E25.3"),sQuery(id+"F0.wireOp",EDGE,"E25.4"),sQuery(id+"F0.wireOp",EDGE,"E25.5"),sQuery(id+"F0.wireOp",EDGE,"E25.6"),sQuery(id+"F0.wireOp",EDGE,"E25.7")])],"isStart":false});
            extrude(context, id + "F17", {"entities" : qUnion([Q0]), "endBound" : BoundingType.UP_TO_SURFACE, "endBoundEntityFace" : qUnion([Q1]), "depth" : 25 * mm});
        }
        {
            var Q0;
            {var subQ0=sQuery(id+"F0.wireOp",EDGE,"E1.bottom");var subQ1=sQuery(id+"F0.wireOp",EDGE,"E1.top");var subQ2=sQuery(id+"F0.wireOp",EDGE,"E1.left");var subQ3=sQuery(id+"F0.wireOp",EDGE,"E1.right");var subQ4=sQuery(id+"F0.wireOp",EDGE,"E4");var subQ5=sQuery(id+"F0.wireOp",EDGE,"E5");var subQ6=sQuery(id+"F0.wireOp",EDGE,"E6");var subQ7=sQuery(id+"F0.wireOp",EDGE,"E7");var subQ8=sQuery(id+"F0.wireOp",EDGE,"E21.filletArc");var subQ9=sQuery(id+"F0.wireOp",EDGE,"E22.filletArc");var subQ10=sQuery(id+"F0.wireOp",EDGE,"E23.filletArc");var subQ11=sQuery(id+"F0.wireOp",EDGE,"E24.filletArc");Q0=makeQuery(id+"F2.boolean.opBoolean","SPLIT",FACE,{"disambiguationData":[TD([makeQuery(id+"F1.opExtrude","SWEPT_FACE",FACE,{"disambiguationData":[OSD([subQ0])]})])],"derivedFrom":makeQuery(id+"F1.opExtrude","CAP_FACE",FACE,{"disambiguationData":[OSD([subQ0,subQ1,subQ2,subQ3,subQ4,subQ5,subQ6,subQ7,subQ8,subQ9,subQ10,subQ11])],"isStart":true})});}
            var Q1;
            Q1=makeQuery(id+"F2.opExtrude","CAP_FACE",FACE,{"disambiguationData":[OSD([sQuery(id+"F0.wireOp",EDGE,"E12"),sQuery(id+"F0.wireOp",EDGE,"E13"),sQuery(id+"F0.wireOp",EDGE,"E14"),sQuery(id+"F0.wireOp",EDGE,"E15"),sQuery(id+"F0.wireOp",EDGE,"E17.filletArc"),sQuery(id+"F0.wireOp",EDGE,"E18.filletArc"),sQuery(id+"F0.wireOp",EDGE,"E19.filletArc"),sQuery(id+"F0.wireOp",EDGE,"E20.filletArc"),sQuery(id+"F0.wireOp",EDGE,"E25.0"),sQuery(id+"F0.wireOp",EDGE,"E25.1"),sQuery(id+"F0.wireOp",EDGE,"E25.2"),sQuery(id+"F0.wireOp",EDGE,"E25.3"),sQuery(id+"F0.wireOp",EDGE,"E25.4"),sQuery(id+"F0.wireOp",EDGE,"E25.5"),sQuery(id+"F0.wireOp",EDGE,"E25.6"),sQuery(id+"F0.wireOp",EDGE,"E25.7")])],"isStart":false});
            extrude(context, id + "F18", {"entities" : qUnion([Q0]), "endBound" : BoundingType.UP_TO_SURFACE, "endBoundEntityFace" : qUnion([Q1]), "depth" : 25 * mm});
        }
    });
